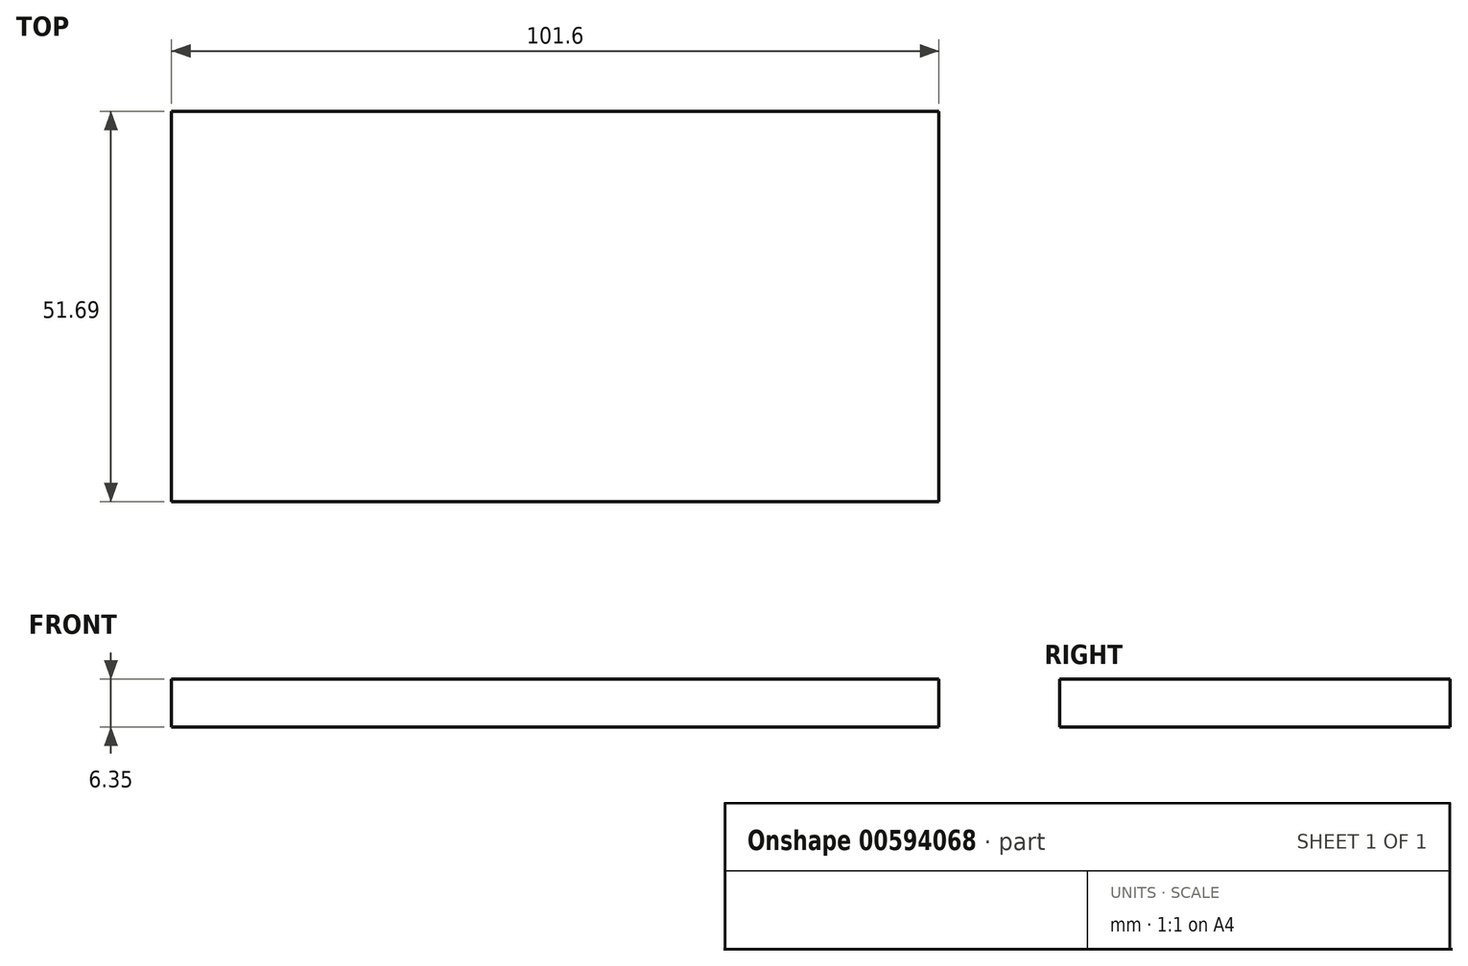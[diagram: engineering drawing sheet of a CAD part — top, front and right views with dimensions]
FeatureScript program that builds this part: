
annotation { "Feature Type Name" : "Feature", "Feature Type Description" : "" }
export const myFeature = defineFeature(function(context is Context, id is Id, definition is map)
    precondition{}
    {
        {
            var Q0;
            Q0=qCreatedBy(makeId("Top.planeOp"),FACE);
            var sketch = newSketch(context, id + "F0", { "sketchPlane" : qUnion([Q0])});
            skLineSegment(sketch, "E0.bottom", {"start": v(0, 0) * mm, "end": v(101.6, 0) * mm});
            skLineSegment(sketch, "E0.top", {"start": v(0, -51.69) * mm, "end": v(101.6, -51.69) * mm});
            skLineSegment(sketch, "E0.left", {"start": v(0, 0) * mm, "end": v(0, -51.69) * mm});
            skLineSegment(sketch, "E0.right", {"start": v(101.6, 0) * mm, "end": v(101.6, -51.69) * mm});
            skSolve(sketch);
        }
        {
            var Q0;
            Q0=makeQuery(id+"F0.imprint","IMPRINT",FACE,{"disambiguationData":[TD([[makeQuery(id+"F0.imprint","IMPRINT",EDGE,{"derivedFrom":sQuery(id+"F0.wireOp",EDGE,"E0.bottom")}),-1.0]])]});
            extrude(context, id + "F1", {"entities" : qUnion([Q0]), "depth" : 6.35 * mm, "offsetDistance" : 25.4 * mm});
        }
    });
